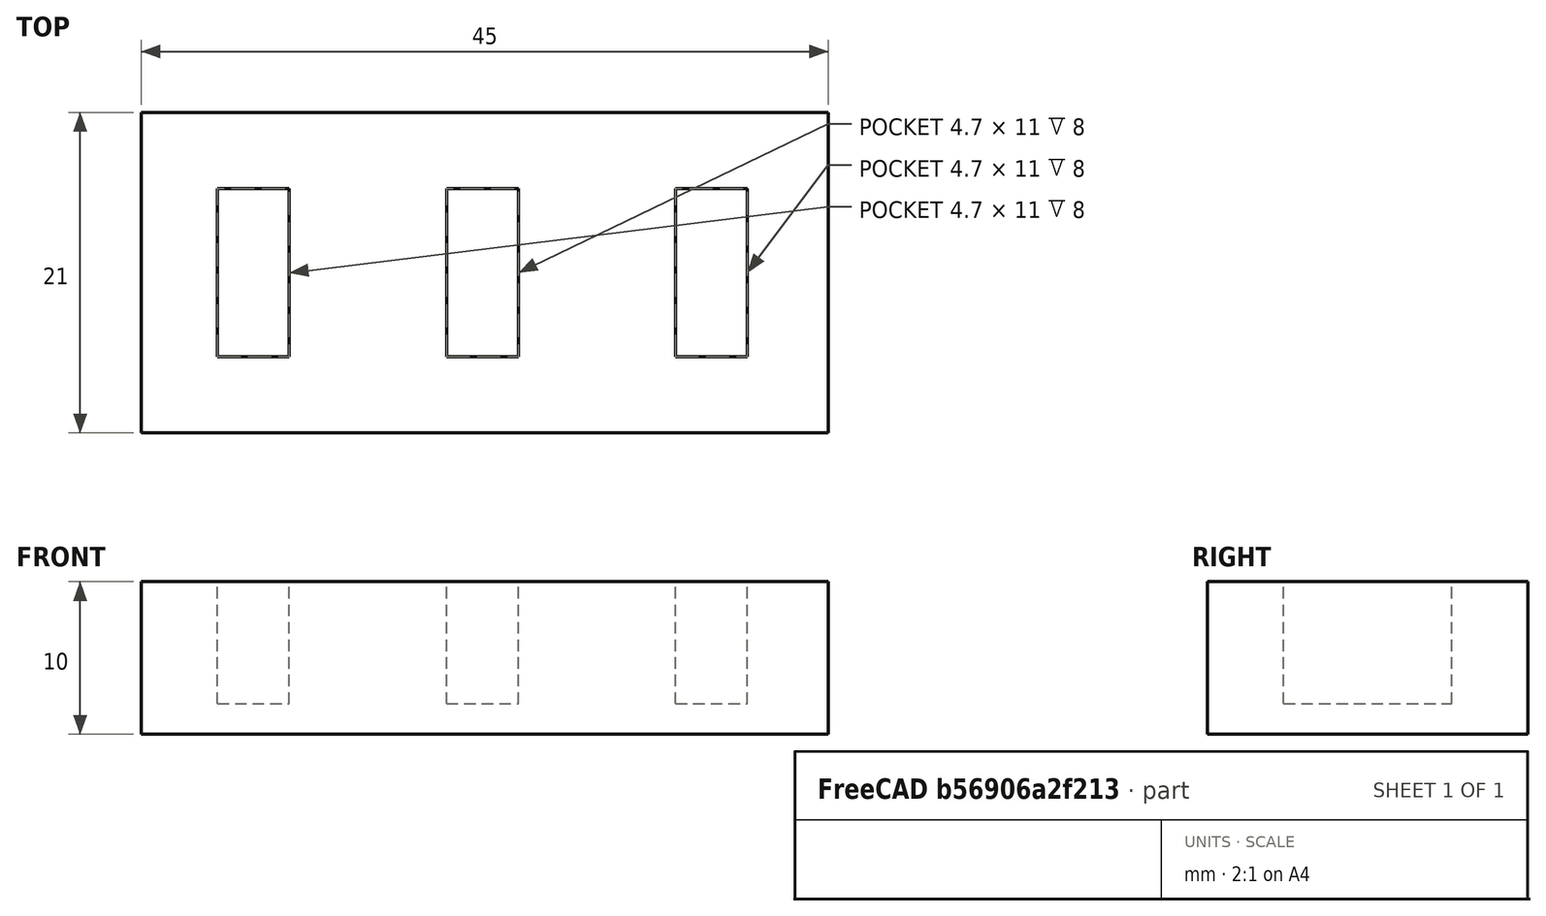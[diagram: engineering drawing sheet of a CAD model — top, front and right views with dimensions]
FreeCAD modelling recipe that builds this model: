
FCSTD DOCUMENT  (FreeCAD 0.16R6707 (Git))
Label: Portapendrives
License: CreativeCommons Attribution-ShareAlike
LicenseURL: http://creativecommons.org/licenses/by-sa/4.0/
objects: Part::Box×4, Part::MultiFuse×1, Part::Cut×1
note: 6 computed .brp shape members not serialized (recipe doc carries the construction recipe); baked Part::Feature solids carry a one-line shape summary decoded from their .brp

FEATURE [Part::Box] Box  label="Ranura-1"
  Height = 12
  Length = 4.7
  Width = 11
FEATURE [Part::Box] Box001  label="Ranura-002"
  Height = 12
  Length = 4.7
  Placement = pos=(15,0,0) rot=(0,0,1;0rad)
  Width = 11
FEATURE [Part::Box] Box002  label="Ranura-003"
  Height = 12
  Length = 4.7
  Placement = pos=(30,0,0) rot=(0,0,1;0rad)
  Width = 11
FEATURE [Part::MultiFuse] Fusion  label="Ranuras"
  Placement = pos=(5,5,2) rot=(0,0,1;0rad)
  Shapes = -> [Box,Box001,Box002]
FEATURE [Part::Box] Box003  label="Base"
  Height = 10
  Length = 45
  Width = 21
FEATURE [Part::Cut] Cut  label="Portapendrives"
  Base = -> Box003
  Tool = -> Fusion
